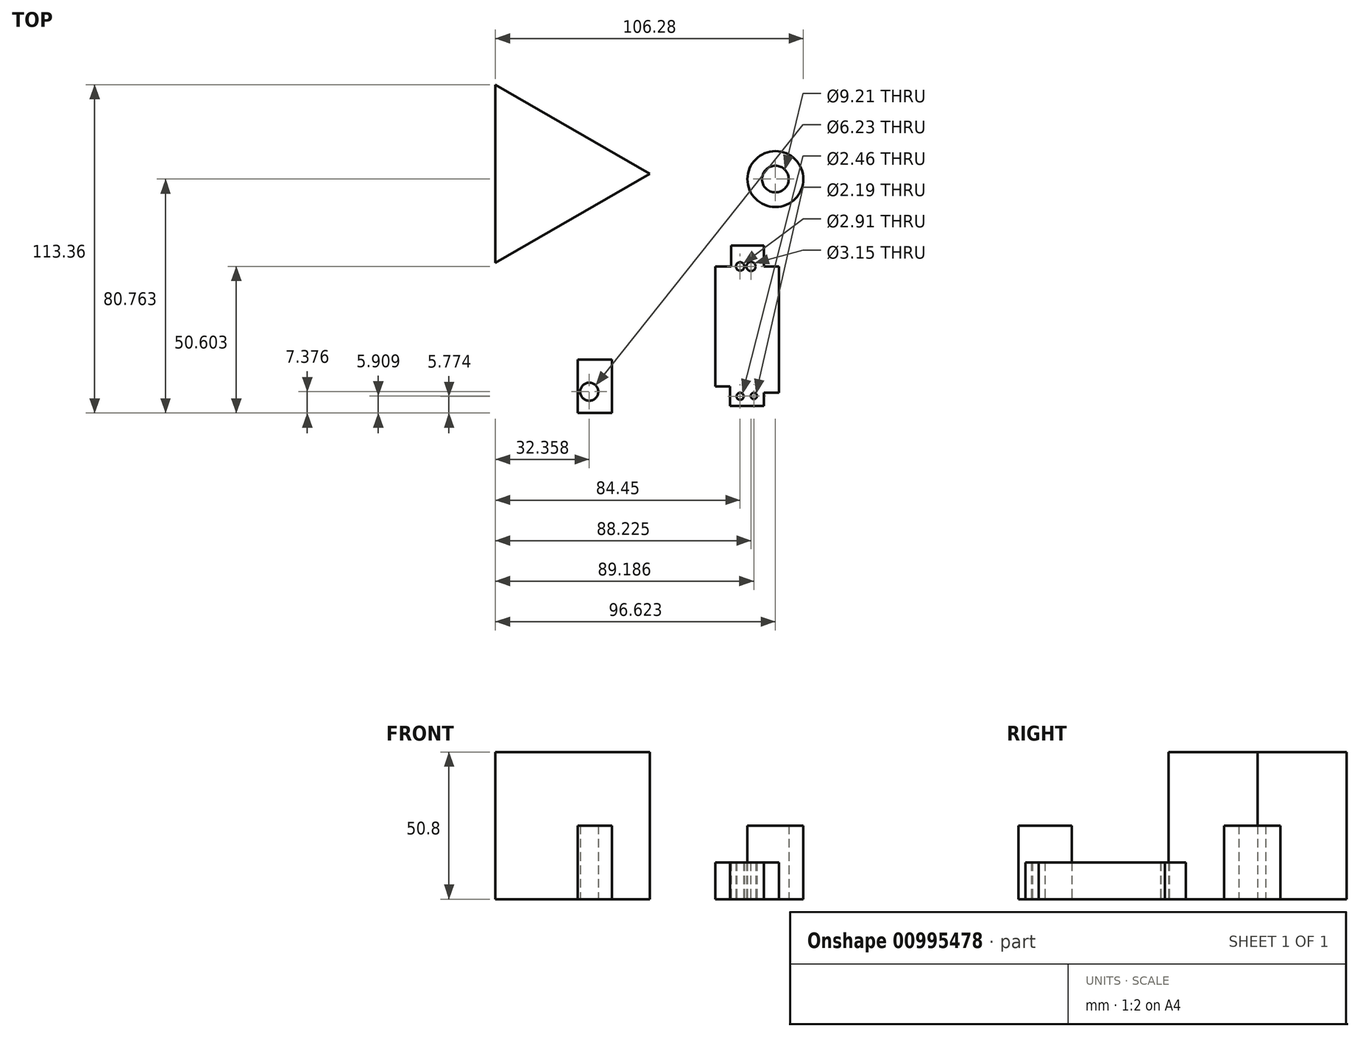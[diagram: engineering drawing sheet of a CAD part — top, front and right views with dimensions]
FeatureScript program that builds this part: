
annotation { "Feature Type Name" : "Feature", "Feature Type Description" : "" }
export const myFeature = defineFeature(function(context is Context, id is Id, definition is map)
    precondition{}
    {
        {
            var Q0;
            Q0=qCreatedBy(makeId("Top.planeOp"),FACE);
            var sketch = newSketch(context, id + "F0", { "sketchPlane" : qUnion([Q0])});
            skLineSegment(sketch, "E0.bottom", {"start": v(-8.54, 25.43) * mm, "end": v(13.44, 25.43) * mm});
            skLineSegment(sketch, "E0.top", {"start": v(-8.54, -29.97) * mm, "end": v(13.44, -29.97) * mm});
            skLineSegment(sketch, "E0.left", {"start": v(-8.54, 25.43) * mm, "end": v(-8.54, -29.97) * mm});
            skLineSegment(sketch, "E0.right", {"start": v(13.44, 25.43) * mm, "end": v(13.44, -29.97) * mm});
            skLineSegment(sketch, "E1.bottom", {"start": v(13.44, 25.43) * mm, "end": v(8.21, 25.43) * mm});
            skLineSegment(sketch, "E1.top", {"start": v(13.44, 18.21) * mm, "end": v(8.21, 18.21) * mm});
            skLineSegment(sketch, "E1.left", {"start": v(13.44, 25.43) * mm, "end": v(13.44, 18.21) * mm});
            skLineSegment(sketch, "E1.right", {"start": v(8.21, 25.43) * mm, "end": v(8.21, 18.21) * mm});
            skLineSegment(sketch, "E2.bottom", {"start": v(-3.05, 25.43) * mm, "end": v(-8.54, 25.43) * mm});
            skLineSegment(sketch, "E2.top", {"start": v(-3.05, 18.21) * mm, "end": v(-8.54, 18.21) * mm});
            skLineSegment(sketch, "E2.left", {"start": v(-3.05, 25.43) * mm, "end": v(-3.05, 18.21) * mm});
            skLineSegment(sketch, "E2.right", {"start": v(-8.54, 25.43) * mm, "end": v(-8.54, 18.21) * mm});
            skLineSegment(sketch, "E3.bottom", {"start": v(-8.54, -23.26) * mm, "end": v(-3.48, -23.26) * mm});
            skLineSegment(sketch, "E3.top", {"start": v(-8.54, -29.97) * mm, "end": v(-3.48, -29.97) * mm});
            skLineSegment(sketch, "E3.left", {"start": v(-8.54, -23.26) * mm, "end": v(-8.54, -29.97) * mm});
            skLineSegment(sketch, "E3.right", {"start": v(-3.48, -23.26) * mm, "end": v(-3.48, -29.97) * mm});
            skLineSegment(sketch, "E4.bottom", {"start": v(13.44, -25.39) * mm, "end": v(8.21, -25.39) * mm});
            skLineSegment(sketch, "E4.top", {"start": v(13.44, -29.97) * mm, "end": v(8.21, -29.97) * mm});
            skLineSegment(sketch, "E4.left", {"start": v(13.44, -25.39) * mm, "end": v(13.44, -29.97) * mm});
            skLineSegment(sketch, "E4.right", {"start": v(8.21, -25.39) * mm, "end": v(8.21, -29.97) * mm});
            skCircle(sketch, "E5", {"center": v(0, -26.62) * mm, "radius": 1.23 * mm});
            skPoint(sketch, "E5.centerSnap0", {"position": v(-3.48, -26.62) * mm});
            skCircle(sketch, "E6", {"center": v(4.74, -26.48) * mm, "radius": 1.1 * mm});
            skCircle(sketch, "E7", {"center": v(0, 18.21) * mm, "radius": 1.46 * mm});
            skCircle(sketch, "E8", {"center": v(3.77, 18.21) * mm, "radius": 1.57 * mm});
            skSolve(sketch);
        }
        {
            var Q0;
            {var subQ3=sQuery(id+"F0.wireOp",EDGE,"E1.top");Q0=makeQuery(id+"F0.imprint","IMPRINT",FACE,{"disambiguationData":[TD([[makeQuery(id+"F0.imprint","IMPRINT",EDGE,{"derivedFrom":subQ3}),1.0]])]});}
            extrude(context, id + "F1", {"entities" : qUnion([Q0]), "depth" : 12.7 * mm, "offsetDistance" : 25.4 * mm});
        }
        {
            var Q0;
            Q0=qCreatedBy(makeId("Top.planeOp"),FACE);
            var sketch = newSketch(context, id + "F2", { "sketchPlane" : qUnion([Q0])});
            skLineSegment(sketch, "E9.bottom", {"start": v(-56.08, -32.39) * mm, "end": v(-44.22, -32.39) * mm});
            skLineSegment(sketch, "E9.top", {"start": v(-56.08, -13.88) * mm, "end": v(-44.22, -13.88) * mm});
            skLineSegment(sketch, "E9.left", {"start": v(-56.08, -32.39) * mm, "end": v(-56.08, -13.88) * mm});
            skLineSegment(sketch, "E9.right", {"start": v(-44.22, -32.39) * mm, "end": v(-44.22, -13.88) * mm});
            skCircle(sketch, "E10", {"center": v(-52.1, -25.01) * mm, "radius": 3.11 * mm});
            skSolve(sketch);
        }
        {
            var Q0;
            Q0=makeQuery(id+"F2.imprint","IMPRINT",FACE,{"disambiguationData":[TD([[makeQuery(id+"F2.imprint","IMPRINT",EDGE,{"derivedFrom":sQuery(id+"F2.wireOp",EDGE,"E9.bottom")}),1.0]])]});
            extrude(context, id + "F3", {"entities" : qUnion([Q0]), "depth" : 25.4 * mm, "offsetDistance" : 25.4 * mm});
        }
        {
            var Q0;
            Q0=qCreatedBy(makeId("Top.planeOp"),FACE);
            var sketch = newSketch(context, id + "F4", { "sketchPlane" : qUnion([Q0])});
            skCircle(sketch, "E11", {"center": v(12.17, 48.37) * mm, "radius": 9.66 * mm});
            skCircle(sketch, "E12", {"center": v(12.17, 48.37) * mm, "radius": 4.6 * mm});
            skSolve(sketch);
        }
        {
            var Q0;
            Q0=makeQuery(id+"F4.imprint","IMPRINT",FACE,{"disambiguationData":[TD([[makeQuery(id+"F4.imprint","IMPRINT",EDGE,{"derivedFrom":sQuery(id+"F4.wireOp",EDGE,"E11")}),1.0]])]});
            extrude(context, id + "F5", {"entities" : qUnion([Q0]), "depth" : 25.4 * mm, "offsetDistance" : 25.4 * mm});
        }
        {
            var Q0;
            Q0=qCreatedBy(makeId("Top.planeOp"),FACE);
            var sketch = newSketch(context, id + "F6", { "sketchPlane" : qUnion([Q0])});
            skCircle(sketch, "E13.cCircle", {"center": v(-66.7, 50.22) * mm, "radius": 17.75 * mm, "construction": true});
            skLineSegment(sketch, "E13.0", {"start": v(-84.45, 19.47) * mm, "end": v(-84.45, 80.97) * mm});
            skLineSegment(sketch, "E13.1", {"start": v(-84.45, 80.97) * mm, "end": v(-31.19, 50.22) * mm});
            skLineSegment(sketch, "E13.2", {"start": v(-31.19, 50.22) * mm, "end": v(-84.45, 19.47) * mm});
            skPoint(sketch, "E13.0.midPoint", {"position": v(-84.45, 50.22) * mm});
            skSolve(sketch);
        }
        {
            var Q0;
            Q0=makeQuery(id+"F6.imprint","IMPRINT",FACE,{"disambiguationData":[TD([[makeQuery(id+"F6.imprint","IMPRINT",EDGE,{"derivedFrom":sQuery(id+"F6.wireOp",EDGE,"E13.0")}),-1.0]])]});
            extrude(context, id + "F7", {"entities" : qUnion([Q0]), "depth" : 50.8 * mm, "offsetDistance" : 25.4 * mm});
        }
    });
